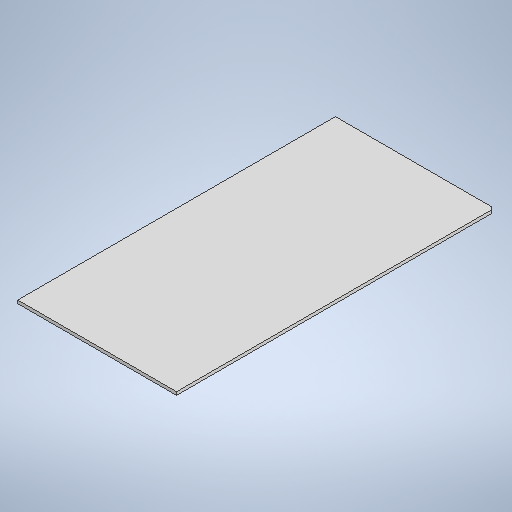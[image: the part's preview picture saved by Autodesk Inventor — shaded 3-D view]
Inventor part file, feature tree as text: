
AUTODESK INVENTOR PART (.ipt)
format: ipt  version: 2025 (Build 290162010, 162A)  size: 293,888 bytes
history: native  units: mm
features: other x4, sketch x2, sheet_metal_op x1, chamfer x1
ambient origin geometry x8: Origin, YZ Plane, XZ Plane, XY Plane, X Axis, Y Axis, Z Axis, Center Point
bodies: Solid1 (feature_tree)
feature tree (8):
  sheet_metal_op  "Face1"
  chamfer  "Chamfer1"  Distance=2.0mm
  other  "Mark1"
  other  "A-Side Definition"
  sketch  "Sketch1"  dims[d0=100.0mm]
  other  "Plate1"
  sketch  "Sketch2"  dims[d1=200.0mm d2=2.0mm d3=2.0mm d4=2.0mm d5=45.0deg]
  other  "Definition1"
